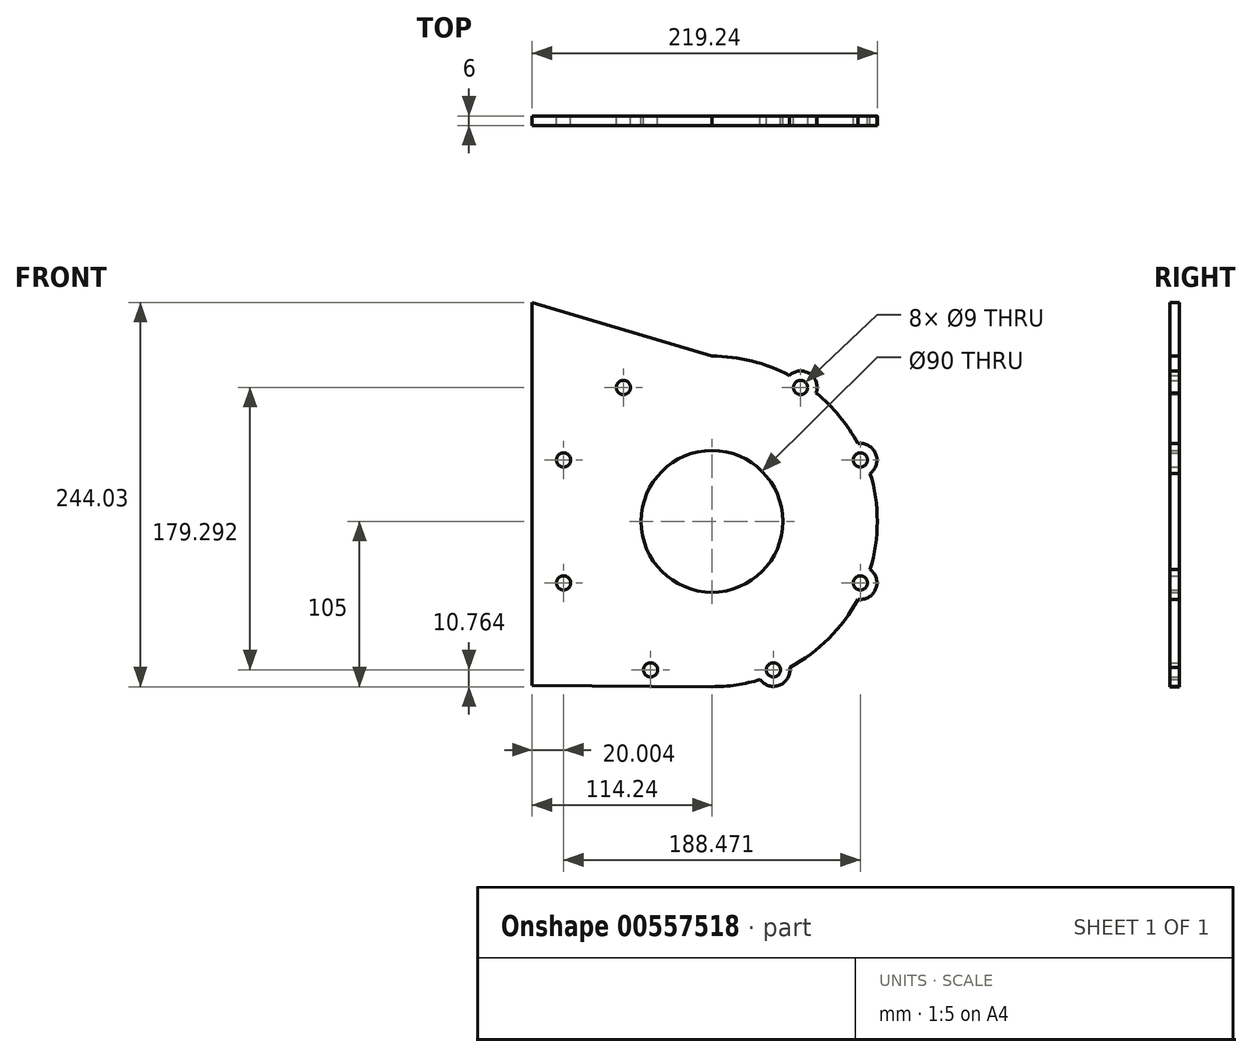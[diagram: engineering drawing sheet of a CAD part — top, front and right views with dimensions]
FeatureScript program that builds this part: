
annotation { "Feature Type Name" : "Feature", "Feature Type Description" : "" }
export const myFeature = defineFeature(function(context is Context, id is Id, definition is map)
    precondition{}
    {
        {
            var Q0;
            Q0=qCreatedBy(makeId("Front.planeOp"),FACE);
            var sketch = newSketch(context, id + "F0", { "sketchPlane" : qUnion([Q0])});
            skCircle(sketch, "E0", {"center": v(0, 0) * mm, "radius": 105 * mm});
            skLineSegment(sketch, "E1", {"start": v(0, 0) * mm, "end": v(39.03, -94.24) * mm});
            skCircle(sketch, "E2", {"center": v(39.03, -94.24) * mm, "radius": 4.5 * mm});
            skLineSegment(sketch, "E3", {"start": v(0, 0) * mm, "end": v(94.24, -39.03) * mm});
            skLineSegment(sketch, "E4", {"start": v(0, 0) * mm, "end": v(94.24, 39.03) * mm});
            skCircle(sketch, "E5", {"center": v(94.24, -39.03) * mm, "radius": 4.5 * mm});
            skCircle(sketch, "E6", {"center": v(94.24, 39.03) * mm, "radius": 4.5 * mm});
            skLineSegment(sketch, "E7", {"start": v(0, 0) * mm, "end": v(56.3, 85.06) * mm});
            skCircle(sketch, "E8", {"center": v(56.3, 85.06) * mm, "radius": 4.5 * mm});
            skLineSegment(sketch, "E9", {"start": v(0, 0) * mm, "end": v(0, 65) * mm, "construction": true});
            skCircle(sketch, "E10.MirrorC", {"center": v(-56.3, 85.06) * mm, "radius": 4.5 * mm});
            skCircle(sketch, "E11.MirrorC", {"center": v(-94.24, 39.03) * mm, "radius": 4.5 * mm});
            skCircle(sketch, "E12.MirrorC", {"center": v(-94.24, -39.03) * mm, "radius": 4.5 * mm});
            skCircle(sketch, "E13.MirrorC", {"center": v(-39.03, -94.24) * mm, "radius": 4.5 * mm});
            skCircle(sketch, "E14", {"center": v(56.3, 85.06) * mm, "radius": 10.5 * mm});
            skCircle(sketch, "E15", {"center": v(94.24, 39.03) * mm, "radius": 10.5 * mm});
            skCircle(sketch, "E16", {"center": v(94.24, -39.03) * mm, "radius": 10.5 * mm});
            skCircle(sketch, "E17", {"center": v(39.03, -94.24) * mm, "radius": 10.5 * mm});
            skCircle(sketch, "E18.MirrorC", {"center": v(-56.3, 85.06) * mm, "radius": 10.5 * mm});
            skCircle(sketch, "E19.MirrorC", {"center": v(-94.24, 39.03) * mm, "radius": 10.5 * mm});
            skCircle(sketch, "E20.MirrorC", {"center": v(-94.24, -39.03) * mm, "radius": 10.5 * mm});
            skCircle(sketch, "E21.MirrorC", {"center": v(-39.03, -94.24) * mm, "radius": 10.5 * mm});
            skLineSegment(sketch, "E22", {"start": v(-94.24, 39.03) * mm, "end": v(-114.24, 39.03) * mm});
            skLineSegment(sketch, "E23", {"start": v(-114.24, 39.03) * mm, "end": v(-114.24, 139.03) * mm});
            skLineSegment(sketch, "E24", {"start": v(-114.24, 139.03) * mm, "end": v(0, 105) * mm});
            skLineSegment(sketch, "E25", {"start": v(-114.24, 39.03) * mm, "end": v(-114.24, -104.23) * mm});
            skLineSegment(sketch, "E26", {"start": v(-114.24, -104.23) * mm, "end": v(0, -105) * mm});
            skCircle(sketch, "E27", {"center": v(0, 0) * mm, "radius": 45 * mm});
            skLineSegment(sketch, "E28", {"start": v(0, 0) * mm, "end": v(-31.01, 0) * mm, "construction": true});
            skSolve(sketch);
        }
        {
            var Q0;
            {var subQ5=sQuery(id+"F0.wireOp",EDGE,"E23");Q0=makeQuery(id+"F0.imprint","IMPRINT",FACE,{"disambiguationData":[TD([[makeQuery(id+"F0.imprint","IMPRINT",EDGE,{"derivedFrom":subQ5}),-1.0]])]});}
            var Q1;
            {var subQ0=sQuery(id+"F0.wireOp",EDGE,"E18.MirrorC");var subQ1=sQuery(id+"F0.wireOp",EDGE,"E0");var subQ2=makeQuery(id+"F0.imprint","INTERSECT",VERTEX,{"disambiguationData":[OD(0.0)],"derivedFrom":[subQ1,subQ0]});Q1=makeQuery(id+"F0.imprint","IMPRINT",FACE,{"disambiguationData":[TD([[makeQuery(id+"F0.imprint","IMPRINT",EDGE,{"disambiguationData":[TD([[subQ2,-1.0]])],"derivedFrom":subQ1}),-1.0]])]});}
            var Q2;
            {var subQ0=sQuery(id+"F0.wireOp",EDGE,"E18.MirrorC");var subQ1=sQuery(id+"F0.wireOp",EDGE,"E0");var subQ2=makeQuery(id+"F0.imprint","INTERSECT",VERTEX,{"disambiguationData":[OD(0.0)],"derivedFrom":[subQ1,subQ0]});Q2=makeQuery(id+"F0.imprint","IMPRINT",FACE,{"disambiguationData":[TD([[makeQuery(id+"F0.imprint","IMPRINT",EDGE,{"disambiguationData":[TD([[subQ2,-1.0]])],"derivedFrom":subQ1}),1.0]])]});}
            var Q3;
            {var subQ0=sQuery(id+"F0.wireOp",EDGE,"E19.MirrorC");var subQ1=sQuery(id+"F0.wireOp",EDGE,"E0");var subQ2=makeQuery(id+"F0.imprint","INTERSECT",VERTEX,{"disambiguationData":[OD(0.0)],"derivedFrom":[subQ1,subQ0]});Q3=makeQuery(id+"F0.imprint","IMPRINT",FACE,{"disambiguationData":[TD([[makeQuery(id+"F0.imprint","IMPRINT",EDGE,{"disambiguationData":[TD([[subQ2,-1.0]])],"derivedFrom":subQ1}),-1.0]])]});}
            var Q4;
            {var subQ0=sQuery(id+"F0.wireOp",EDGE,"E11.MirrorC");var subQ1=sQuery(id+"F0.wireOp",EDGE,"E0");var subQ2=makeQuery(id+"F0.imprint","INTERSECT",VERTEX,{"disambiguationData":[OD(1.0)],"derivedFrom":[subQ1,subQ0]});Q4=makeQuery(id+"F0.imprint","IMPRINT",FACE,{"disambiguationData":[TD([[makeQuery(id+"F0.imprint","IMPRINT",EDGE,{"disambiguationData":[TD([[subQ2,-1.0]])],"derivedFrom":subQ1}),-1.0]])]});}
            var Q5;
            {var subQ0=sQuery(id+"F0.wireOp",EDGE,"E19.MirrorC");var subQ1=sQuery(id+"F0.wireOp",EDGE,"E0");var subQ2=makeQuery(id+"F0.imprint","INTERSECT",VERTEX,{"disambiguationData":[OD(0.0)],"derivedFrom":[subQ1,subQ0]});Q5=makeQuery(id+"F0.imprint","IMPRINT",FACE,{"disambiguationData":[TD([[makeQuery(id+"F0.imprint","IMPRINT",EDGE,{"disambiguationData":[TD([[subQ2,-1.0]])],"derivedFrom":subQ1}),1.0]])]});}
            var Q6;
            {var subQ8=sQuery(id+"F0.wireOp",EDGE,"E25");Q6=makeQuery(id+"F0.imprint","IMPRINT",FACE,{"disambiguationData":[TD([[makeQuery(id+"F0.imprint","IMPRINT",EDGE,{"derivedFrom":subQ8}),1.0]])]});}
            var Q7;
            {var subQ0=sQuery(id+"F0.wireOp",EDGE,"E20.MirrorC");var subQ1=sQuery(id+"F0.wireOp",EDGE,"E0");var subQ2=makeQuery(id+"F0.imprint","INTERSECT",VERTEX,{"disambiguationData":[OD(0.0)],"derivedFrom":[subQ1,subQ0]});Q7=makeQuery(id+"F0.imprint","IMPRINT",FACE,{"disambiguationData":[TD([[makeQuery(id+"F0.imprint","IMPRINT",EDGE,{"disambiguationData":[TD([[subQ2,-1.0]])],"derivedFrom":subQ1}),-1.0]])]});}
            var Q8;
            {var subQ0=sQuery(id+"F0.wireOp",EDGE,"E20.MirrorC");var subQ1=sQuery(id+"F0.wireOp",EDGE,"E0");var subQ2=makeQuery(id+"F0.imprint","INTERSECT",VERTEX,{"disambiguationData":[OD(0.0)],"derivedFrom":[subQ1,subQ0]});Q8=makeQuery(id+"F0.imprint","IMPRINT",FACE,{"disambiguationData":[TD([[makeQuery(id+"F0.imprint","IMPRINT",EDGE,{"disambiguationData":[TD([[subQ2,-1.0]])],"derivedFrom":subQ1}),1.0]])]});}
            var Q9;
            {var subQ1=sQuery(id+"F0.wireOp",EDGE,"E0");var subQ19=makeQuery(id+"F0.imprint","INTERSECT",VERTEX,{"derivedFrom":[subQ1,sQuery(id+"F0.wireOp",EDGE,"E24")]});Q9=makeQuery(id+"F0.imprint","IMPRINT",FACE,{"disambiguationData":[TD([[makeQuery(id+"F0.imprint","IMPRINT",EDGE,{"disambiguationData":[TD([[subQ19,1.0]])],"derivedFrom":subQ1}),1.0]])]});}
            var Q10;
            {var subQ0=sQuery(id+"F0.wireOp",EDGE,"E21.MirrorC");var subQ1=sQuery(id+"F0.wireOp",EDGE,"E0");var subQ2=makeQuery(id+"F0.imprint","INTERSECT",VERTEX,{"disambiguationData":[OD(0.0)],"derivedFrom":[subQ1,subQ0]});Q10=makeQuery(id+"F0.imprint","IMPRINT",FACE,{"disambiguationData":[TD([[makeQuery(id+"F0.imprint","IMPRINT",EDGE,{"disambiguationData":[TD([[subQ2,-1.0]])],"derivedFrom":subQ1}),1.0]])]});}
            var Q11;
            {var subQ0=sQuery(id+"F0.wireOp",EDGE,"E21.MirrorC");var subQ2=sQuery(id+"F0.wireOp",EDGE,"E0");var subQ7=makeQuery(id+"F0.imprint","INTERSECT",VERTEX,{"disambiguationData":[OD(0.0)],"derivedFrom":[subQ2,subQ0]});Q11=makeQuery(id+"F0.imprint","IMPRINT",FACE,{"disambiguationData":[TD([[makeQuery(id+"F0.imprint","IMPRINT",EDGE,{"disambiguationData":[TD([[subQ7,-1.0]])],"derivedFrom":subQ2}),-1.0]])]});}
            var Q12;
            {var subQ0=sQuery(id+"F0.wireOp",EDGE,"E26");var subQ1=sQuery(id+"F0.wireOp",EDGE,"E0");var subQ2=makeQuery(id+"F0.imprint","INTERSECT",VERTEX,{"disambiguationData":[OD(1.0)],"derivedFrom":[subQ1,subQ0]});Q12=makeQuery(id+"F0.imprint","IMPRINT",FACE,{"disambiguationData":[TD([[makeQuery(id+"F0.imprint","IMPRINT",EDGE,{"disambiguationData":[TD([[subQ2,1.0]])],"derivedFrom":subQ1}),-1.0]])]});}
            var Q13;
            {var subQ0=sQuery(id+"F0.wireOp",EDGE,"E17");var subQ1=sQuery(id+"F0.wireOp",EDGE,"E0");var subQ2=makeQuery(id+"F0.imprint","INTERSECT",VERTEX,{"disambiguationData":[OD(0.0)],"derivedFrom":[subQ1,subQ0]});Q13=makeQuery(id+"F0.imprint","IMPRINT",FACE,{"disambiguationData":[TD([[makeQuery(id+"F0.imprint","IMPRINT",EDGE,{"disambiguationData":[TD([[subQ2,-1.0]])],"derivedFrom":subQ1}),1.0]])]});}
            var Q14;
            {var subQ0=sQuery(id+"F0.wireOp",EDGE,"E17");var subQ1=sQuery(id+"F0.wireOp",EDGE,"E0");var subQ2=makeQuery(id+"F0.imprint","INTERSECT",VERTEX,{"disambiguationData":[OD(1.0)],"derivedFrom":[subQ1,subQ0]});Q14=makeQuery(id+"F0.imprint","IMPRINT",FACE,{"disambiguationData":[TD([[makeQuery(id+"F0.imprint","IMPRINT",EDGE,{"disambiguationData":[TD([[subQ2,1.0]])],"derivedFrom":subQ1}),1.0]])]});}
            var Q15;
            {var subQ0=sQuery(id+"F0.wireOp",EDGE,"E17");var subQ1=sQuery(id+"F0.wireOp",EDGE,"E0");var subQ2=makeQuery(id+"F0.imprint","INTERSECT",VERTEX,{"disambiguationData":[OD(0.0)],"derivedFrom":[subQ1,subQ0]});Q15=makeQuery(id+"F0.imprint","IMPRINT",FACE,{"disambiguationData":[TD([[makeQuery(id+"F0.imprint","IMPRINT",EDGE,{"disambiguationData":[TD([[subQ2,-1.0]])],"derivedFrom":subQ1}),-1.0]])]});}
            var Q16;
            {var subQ1=sQuery(id+"F0.wireOp",EDGE,"E0");var subQ7=sQuery(id+"F0.wireOp",EDGE,"E17");var subQ8=makeQuery(id+"F0.imprint","INTERSECT",VERTEX,{"disambiguationData":[OD(1.0)],"derivedFrom":[subQ1,subQ7]});Q16=makeQuery(id+"F0.imprint","IMPRINT",FACE,{"disambiguationData":[TD([[makeQuery(id+"F0.imprint","IMPRINT",EDGE,{"disambiguationData":[TD([[subQ8,-1.0]])],"derivedFrom":subQ1}),1.0]])]});}
            var Q17;
            {var subQ0=sQuery(id+"F0.wireOp",EDGE,"E15");var subQ1=sQuery(id+"F0.wireOp",EDGE,"E0");var subQ2=makeQuery(id+"F0.imprint","INTERSECT",VERTEX,{"disambiguationData":[OD(0.0)],"derivedFrom":[subQ1,subQ0]});Q17=makeQuery(id+"F0.imprint","IMPRINT",FACE,{"disambiguationData":[TD([[makeQuery(id+"F0.imprint","IMPRINT",EDGE,{"disambiguationData":[TD([[subQ2,1.0]])],"derivedFrom":subQ1}),1.0]])]});}
            var Q18;
            {var subQ1=sQuery(id+"F0.wireOp",EDGE,"E0");var subQ7=sQuery(id+"F0.wireOp",EDGE,"E15");var subQ9=makeQuery(id+"F0.imprint","INTERSECT",VERTEX,{"disambiguationData":[OD(1.0)],"derivedFrom":[subQ1,subQ7]});Q18=makeQuery(id+"F0.imprint","IMPRINT",FACE,{"disambiguationData":[TD([[makeQuery(id+"F0.imprint","IMPRINT",EDGE,{"disambiguationData":[TD([[subQ9,-1.0]])],"derivedFrom":subQ1}),1.0]])]});}
            var Q19;
            {var subQ0=sQuery(id+"F0.wireOp",EDGE,"E14");var subQ1=sQuery(id+"F0.wireOp",EDGE,"E0");var subQ2=makeQuery(id+"F0.imprint","INTERSECT",VERTEX,{"disambiguationData":[OD(0.0)],"derivedFrom":[subQ1,subQ0]});Q19=makeQuery(id+"F0.imprint","IMPRINT",FACE,{"disambiguationData":[TD([[makeQuery(id+"F0.imprint","IMPRINT",EDGE,{"disambiguationData":[TD([[subQ2,-1.0]])],"derivedFrom":subQ1}),-1.0]])]});}
            var Q20;
            {var subQ0=sQuery(id+"F0.wireOp",EDGE,"E14");var subQ1=sQuery(id+"F0.wireOp",EDGE,"E0");var subQ2=makeQuery(id+"F0.imprint","INTERSECT",VERTEX,{"disambiguationData":[OD(1.0)],"derivedFrom":[subQ1,subQ0]});Q20=makeQuery(id+"F0.imprint","IMPRINT",FACE,{"disambiguationData":[TD([[makeQuery(id+"F0.imprint","IMPRINT",EDGE,{"disambiguationData":[TD([[subQ2,1.0]])],"derivedFrom":subQ1}),1.0]])]});}
            var Q21;
            {var subQ0=sQuery(id+"F0.wireOp",EDGE,"E14");var subQ1=sQuery(id+"F0.wireOp",EDGE,"E0");var subQ2=makeQuery(id+"F0.imprint","INTERSECT",VERTEX,{"disambiguationData":[OD(0.0)],"derivedFrom":[subQ1,subQ0]});Q21=makeQuery(id+"F0.imprint","IMPRINT",FACE,{"disambiguationData":[TD([[makeQuery(id+"F0.imprint","IMPRINT",EDGE,{"disambiguationData":[TD([[subQ2,-1.0]])],"derivedFrom":subQ1}),1.0]])]});}
            var Q22;
            {var subQ0=sQuery(id+"F0.wireOp",EDGE,"E15");var subQ1=sQuery(id+"F0.wireOp",EDGE,"E0");var subQ2=makeQuery(id+"F0.imprint","INTERSECT",VERTEX,{"disambiguationData":[OD(1.0)],"derivedFrom":[subQ1,subQ0]});Q22=makeQuery(id+"F0.imprint","IMPRINT",FACE,{"disambiguationData":[TD([[makeQuery(id+"F0.imprint","IMPRINT",EDGE,{"disambiguationData":[TD([[subQ2,1.0]])],"derivedFrom":subQ1}),1.0]])]});}
            var Q23;
            {var subQ0=sQuery(id+"F0.wireOp",EDGE,"E16");var subQ1=sQuery(id+"F0.wireOp",EDGE,"E0");var subQ2=makeQuery(id+"F0.imprint","INTERSECT",VERTEX,{"disambiguationData":[OD(1.0)],"derivedFrom":[subQ1,subQ0]});Q23=makeQuery(id+"F0.imprint","IMPRINT",FACE,{"disambiguationData":[TD([[makeQuery(id+"F0.imprint","IMPRINT",EDGE,{"disambiguationData":[TD([[subQ2,1.0]])],"derivedFrom":subQ1}),1.0]])]});}
            var Q24;
            {var subQ0=sQuery(id+"F0.wireOp",EDGE,"E16");var subQ1=sQuery(id+"F0.wireOp",EDGE,"E0");var subQ2=makeQuery(id+"F0.imprint","INTERSECT",VERTEX,{"disambiguationData":[OD(0.0)],"derivedFrom":[subQ1,subQ0]});Q24=makeQuery(id+"F0.imprint","IMPRINT",FACE,{"disambiguationData":[TD([[makeQuery(id+"F0.imprint","IMPRINT",EDGE,{"disambiguationData":[TD([[subQ2,-1.0]])],"derivedFrom":subQ1}),1.0]])]});}
            var Q25;
            {var subQ0=sQuery(id+"F0.wireOp",EDGE,"E16");var subQ1=sQuery(id+"F0.wireOp",EDGE,"E0");var subQ2=makeQuery(id+"F0.imprint","INTERSECT",VERTEX,{"disambiguationData":[OD(0.0)],"derivedFrom":[subQ1,subQ0]});Q25=makeQuery(id+"F0.imprint","IMPRINT",FACE,{"disambiguationData":[TD([[makeQuery(id+"F0.imprint","IMPRINT",EDGE,{"disambiguationData":[TD([[subQ2,-1.0]])],"derivedFrom":subQ1}),-1.0]])]});}
            var Q26;
            {var subQ0=sQuery(id+"F0.wireOp",EDGE,"E15");var subQ1=sQuery(id+"F0.wireOp",EDGE,"E0");var subQ2=makeQuery(id+"F0.imprint","INTERSECT",VERTEX,{"disambiguationData":[OD(0.0)],"derivedFrom":[subQ1,subQ0]});Q26=makeQuery(id+"F0.imprint","IMPRINT",FACE,{"disambiguationData":[TD([[makeQuery(id+"F0.imprint","IMPRINT",EDGE,{"disambiguationData":[TD([[subQ2,-1.0]])],"derivedFrom":subQ1}),-1.0]])]});}
            var Q27;
            {var subQ0=sQuery(id+"F0.wireOp",EDGE,"E15");var subQ1=sQuery(id+"F0.wireOp",EDGE,"E0");var subQ2=makeQuery(id+"F0.imprint","INTERSECT",VERTEX,{"disambiguationData":[OD(0.0)],"derivedFrom":[subQ1,subQ0]});Q27=makeQuery(id+"F0.imprint","IMPRINT",FACE,{"disambiguationData":[TD([[makeQuery(id+"F0.imprint","IMPRINT",EDGE,{"disambiguationData":[TD([[subQ2,-1.0]])],"derivedFrom":subQ1}),1.0]])]});}
            extrude(context, id + "F1", {"entities" : qUnion([Q0, Q1, Q2, Q3, Q4, Q5, Q6, Q7, Q8, Q9, Q10, Q11, Q12, Q13, Q14, Q15, Q16, Q17, Q18, Q19, Q20, Q21, Q22, Q23, Q24, Q25, Q26, Q27]), "depth" : 6 * mm, "offsetDistance" : 25 * mm});
        }
    });
